# Revit family: EKF_EE_КомплектПластроновГлухихUNIT_PROxima
name_source: partatom
category: Электрооборудование
units: mm (PartAtom-declared; Revit-internal decimal feet)

## family parameters
Всегда вертикально = Нет
На основе рабочей плоскости = Да
Общий = Да
При загрузке вырезать с полостями = Нет
Размер круглого соединителя = Использовать диаметр
Тип детали = Силовой щит
Точка расчета площади = Нет

## types (9) — shared parameters
ADSK_Единица измерения = шт.
ADSK_Завод-изготовитель = EKF
ADSK_Количество = 1
ADSK_Марка = Комплект пластронов глухих (3шт.)
ADSK_Материал = Сталь, с порошковым покрытием, белый
ADSK_Обозначение = Комплект пластронов глухих (3шт.)
ADSK_Размер_Глубина = 8 мм
D = 7 мм
t = 1.2 мм
Глубина = 8 мм
Изготовитель = EKF
Отв_Кол = 2
Отступ = 11 мм
ОтступВ = 24 мм
Серия номенклатуры = Unit PROxima
Степень защиты IP = -
ТВ = EKF_2
Тип установки = -
zero-valued in all types: ADSK_Масса, Отметка по умолчанию

## per-type parameters (varying)
| type | ADSK_Код изделия | ADSK_Размер_Высота | ADSK_Размер_Ширина | Высота | Тип |
| Комплект пластронов глухих (3шт.) высотой 200мм для ВРУ Unit шириной 450мм EKF PROxima | mb-15-gp-2045 | 198 мм | 332 мм | 193 мм | 27 мм |
| Комплект пластронов глухих (3шт.) высотой 200мм для ВРУ Unit шириной 600мм EKF PROxima | mb-15-gp-2060 | 198 мм | 482 мм | 193 мм | 28 мм |
| Комплект пластронов глухих (3шт.) высотой 200мм для ВРУ Unit шириной 800мм EKF PROxima | mb-15-gp-2080 | 198 мм | 682 мм | 193 мм | 29 мм |
| Комплект пластронов глухих (3шт.) высотой 300 мм для ВРУ Unit шириной 450 мм EKF PROxima | mb-15-gp-3045 | 298 мм | 332 мм | 293 мм | 30 мм |
| Комплект пластронов глухих (3шт.) высотой 300 мм для ВРУ Unit шириной 600 мм EKF PROxima | mb-15-gp-3060 | 298 мм | 482 мм | 293 мм | 31 мм |
| Комплект пластронов глухих (3шт.) высотой 300 мм для ВРУ Unit шириной 800 мм EKF PROxima | mb-15-gp-3080 | 298 мм | 682 мм | 293 мм | 32 мм |
| Комплект пластронов глухих (3шт.) высотой 500 мм для ВРУ Unit шириной 450 мм EKF PROxima | mb-15-gp-5045 | 498 мм | 332 мм | 493 мм | 33 мм |
| Комплект пластронов глухих (3шт.) высотой 500 мм для ВРУ Unit шириной 600 мм EKF PROxima | mb-15-gp-5060 | 498 мм | 482 мм | 493 мм | 34 мм |
| Комплект пластронов глухих (3шт.) высотой 500 мм для ВРУ Unit шириной 800 мм EKF PROxima | mb-15-gp-5080 | 498 мм | 682 мм | 493 мм | 35 мм |

note: column(s) folded — value = type name in every type: ADSK_Наименование
